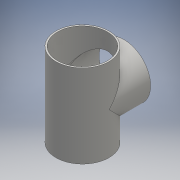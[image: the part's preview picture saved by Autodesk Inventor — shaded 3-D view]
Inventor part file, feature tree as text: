
AUTODESK INVENTOR PART (.ipt)
format: ipt  version: 2016 (Build 200138000, 138)  size: 149,504 bytes
history: native  units: mm
features: extrude x4, sketch x4, projected_geometry x1
ambient origin geometry x8: Origin, YZ Plane, XZ Plane, XY Plane, X Axis, Y Axis, Z Axis, Center Point
bodies: Solid1 (feature_tree)
feature tree (9):
  extrude  "Extrusion1"  Depth=9.52mm
  extrude  "Extrusion2"  Depth=9.52mm
  extrude  "Extrusion3"  Depth=254.0mm TaperAngle=0.0deg
  extrude  "Extrusion4"  Depth=254.0mm TaperAngle=0.0deg
  sketch  "Sketch1"  dims[d0=324.0mm d1=9.52mm]
  sketch  "Sketch2"  dims[d2=508.0mm d3=0.0mm d4=9.52mm]
  sketch  "Sketch3"  dims[d5=324.0mm d6=254.0mm d7=0.0mm]
  sketch  "Sketch4"  dims[d8=254.0mm d9=0.0mm d10=254.0mm d11=0.0mm]
  projected_geometry  "Projected Loop1"
